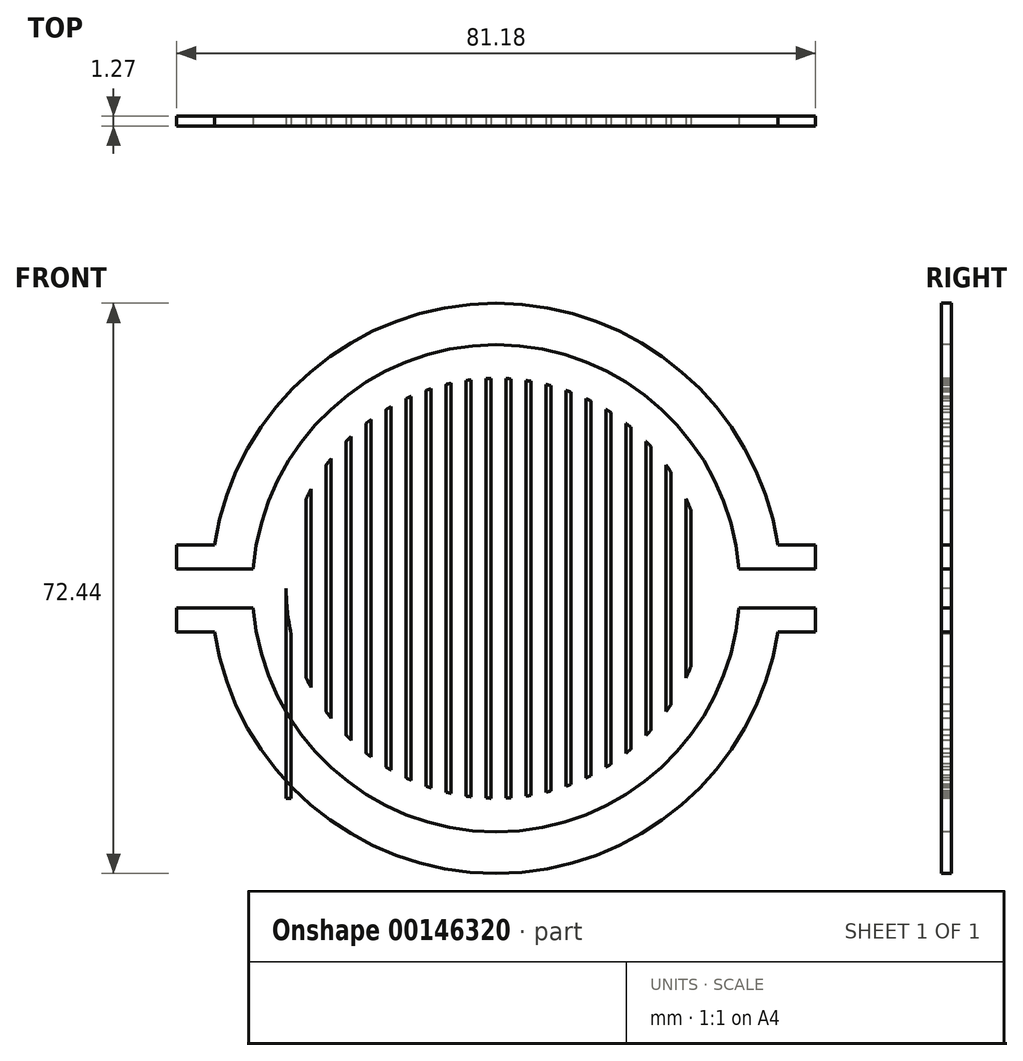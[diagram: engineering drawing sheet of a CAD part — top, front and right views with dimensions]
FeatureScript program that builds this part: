
annotation { "Feature Type Name" : "Feature", "Feature Type Description" : "" }
export const myFeature = defineFeature(function(context is Context, id is Id, definition is map)
    precondition{}
    {
        {
            var Q0;
            Q0=qCreatedBy(makeId("Front.planeOp"),FACE);
            var sketch = newSketch(context, id + "F0", { "sketchPlane" : qUnion([Q0])});
            skPoint(sketch, "E0", {"position": v(0.63, 25.4) * mm});
            skPoint(sketch, "E1", {"position": v(-0.64, 25.4) * mm});
            skLineSegment(sketch, "E2", {"start": v(-0.64, 25.4) * mm, "end": v(0.63, 25.4) * mm});
            skLineSegment(sketch, "E3", {"start": v(0.63, 25.4) * mm, "end": v(0.63, 0.46) * mm});
            skLineSegment(sketch, "E4", {"start": v(-0.64, 25.4) * mm, "end": v(-0.64, 0.2) * mm});
            skPoint(sketch, "E5.1.0", {"position": v(-14.42, 20.92) * mm});
            skLineSegment(sketch, "E5.1.1", {"start": v(-14.42, 20.92) * mm, "end": v(-0.64, 1.95) * mm});
            skLineSegment(sketch, "E5.1.2", {"start": v(-15.44, 20.18) * mm, "end": v(-1.66, 1.2) * mm});
            skPoint(sketch, "E5.1.3", {"position": v(-15.44, 20.18) * mm});
            skLineSegment(sketch, "E5.1.4", {"start": v(-15.44, 20.18) * mm, "end": v(-14.42, 20.92) * mm});
            skPoint(sketch, "E5.2.0", {"position": v(-23.96, 8.45) * mm});
            skLineSegment(sketch, "E5.2.1", {"start": v(-23.96, 8.45) * mm, "end": v(-1.66, 1.2) * mm});
            skLineSegment(sketch, "E5.2.2", {"start": v(-24.35, 7.25) * mm, "end": v(-2.05, 0) * mm});
            skPoint(sketch, "E5.2.3", {"position": v(-24.35, 7.25) * mm});
            skLineSegment(sketch, "E5.2.4", {"start": v(-24.35, 7.25) * mm, "end": v(-23.96, 8.45) * mm});
            skPoint(sketch, "E5.3.0", {"position": v(-24.35, -7.25) * mm});
            skLineSegment(sketch, "E5.3.1", {"start": v(-24.35, -7.25) * mm, "end": v(-2.05, 0) * mm});
            skLineSegment(sketch, "E5.3.2", {"start": v(-23.96, -8.45) * mm, "end": v(-1.66, -1.2) * mm});
            skPoint(sketch, "E5.3.3", {"position": v(-23.96, -8.45) * mm});
            skLineSegment(sketch, "E5.3.4", {"start": v(-23.96, -8.45) * mm, "end": v(-24.35, -7.25) * mm});
            skPoint(sketch, "E5.4.0", {"position": v(-15.44, -20.18) * mm});
            skLineSegment(sketch, "E5.4.1", {"start": v(-15.44, -20.18) * mm, "end": v(-1.66, -1.2) * mm});
            skLineSegment(sketch, "E5.4.2", {"start": v(-14.42, -20.92) * mm, "end": v(-0.63, -1.95) * mm});
            skPoint(sketch, "E5.4.3", {"position": v(-14.42, -20.92) * mm});
            skLineSegment(sketch, "E5.4.4", {"start": v(-14.42, -20.92) * mm, "end": v(-15.44, -20.18) * mm});
            skPoint(sketch, "E5.5.0", {"position": v(-0.64, -25.4) * mm});
            skLineSegment(sketch, "E5.5.1", {"start": v(-0.64, -25.4) * mm, "end": v(-0.63, -1.95) * mm});
            skLineSegment(sketch, "E5.5.2", {"start": v(0.63, -25.4) * mm, "end": v(0.64, -1.95) * mm});
            skPoint(sketch, "E5.5.3", {"position": v(0.63, -25.4) * mm});
            skLineSegment(sketch, "E5.5.4", {"start": v(0.63, -25.4) * mm, "end": v(-0.64, -25.4) * mm});
            skPoint(sketch, "E5.6.0", {"position": v(14.42, -20.92) * mm});
            skLineSegment(sketch, "E5.6.1", {"start": v(14.42, -20.92) * mm, "end": v(0.63, -1.95) * mm});
            skLineSegment(sketch, "E5.6.2", {"start": v(15.44, -20.18) * mm, "end": v(1.66, -1.2) * mm});
            skPoint(sketch, "E5.6.3", {"position": v(15.44, -20.18) * mm});
            skLineSegment(sketch, "E5.6.4", {"start": v(15.44, -20.18) * mm, "end": v(14.42, -20.92) * mm});
            skPoint(sketch, "E5.7.0", {"position": v(23.96, -8.45) * mm});
            skLineSegment(sketch, "E5.7.1", {"start": v(23.96, -8.45) * mm, "end": v(1.66, -1.2) * mm});
            skLineSegment(sketch, "E5.7.2", {"start": v(24.35, -7.25) * mm, "end": v(2.05, 0) * mm});
            skPoint(sketch, "E5.7.3", {"position": v(24.35, -7.25) * mm});
            skLineSegment(sketch, "E5.7.4", {"start": v(24.35, -7.25) * mm, "end": v(23.96, -8.45) * mm});
            skPoint(sketch, "E5.8.0", {"position": v(24.35, 7.25) * mm});
            skLineSegment(sketch, "E5.8.1", {"start": v(24.35, 7.25) * mm, "end": v(2.05, 0) * mm});
            skLineSegment(sketch, "E5.8.2", {"start": v(23.96, 8.45) * mm, "end": v(1.66, 1.2) * mm});
            skPoint(sketch, "E5.8.3", {"position": v(23.96, 8.45) * mm});
            skLineSegment(sketch, "E5.8.4", {"start": v(23.96, 8.45) * mm, "end": v(24.35, 7.25) * mm});
            skPoint(sketch, "E5.9.0", {"position": v(15.44, 20.18) * mm});
            skLineSegment(sketch, "E5.9.1", {"start": v(15.44, 20.18) * mm, "end": v(1.66, 1.2) * mm});
            skLineSegment(sketch, "E5.9.2", {"start": v(14.42, 20.92) * mm, "end": v(0.63, 1.95) * mm});
            skPoint(sketch, "E5.9.3", {"position": v(14.42, 20.92) * mm});
            skLineSegment(sketch, "E5.9.4", {"start": v(14.42, 20.92) * mm, "end": v(15.44, 20.18) * mm});
            skPoint(sketch, "E5.center", {"position": v(0, 0) * mm});
            skLineSegment(sketch, "E6.trimOffspring", {"start": v(0.63, 0.87) * mm, "end": v(0.24, 0.75) * mm});
            skLineSegment(sketch, "E7.trimOffspring", {"start": v(1.03, 0.33) * mm, "end": v(0.78, 0) * mm});
            skLineSegment(sketch, "E8.trimOffspring", {"start": v(1.03, 0.33) * mm, "end": v(0.63, 0.46) * mm});
            skLineSegment(sketch, "E9.trimOffspring", {"start": v(1.03, -0.33) * mm, "end": v(0.64, -0.46) * mm});
            skLineSegment(sketch, "E10.trimOffspring", {"start": v(1.03, -0.33) * mm, "end": v(0.78, 0) * mm});
            skLineSegment(sketch, "E11.trimOffspring", {"start": v(0.64, -0.87) * mm, "end": v(0.24, -0.75) * mm});
            skLineSegment(sketch, "E12.trimOffspring", {"start": v(0.64, -0.87) * mm, "end": v(0.64, -0.46) * mm});
            skLineSegment(sketch, "E13.trimOffspring", {"start": v(0, -1.08) * mm, "end": v(-0.24, -0.75) * mm});
            skLineSegment(sketch, "E14.trimOffspring", {"start": v(0, -1.08) * mm, "end": v(0.24, -0.75) * mm});
            skLineSegment(sketch, "E15.trimOffspring", {"start": v(-0.63, -0.87) * mm, "end": v(-0.63, -0.46) * mm});
            skLineSegment(sketch, "E16.trimOffspring", {"start": v(-0.63, -0.87) * mm, "end": v(-0.24, -0.75) * mm});
            skLineSegment(sketch, "E17.trimOffspring", {"start": v(-1.03, -0.33) * mm, "end": v(-0.78, 0) * mm});
            skLineSegment(sketch, "E18.trimOffspring", {"start": v(-1.03, -0.33) * mm, "end": v(-0.63, -0.46) * mm});
            skLineSegment(sketch, "E19.trimOffspring", {"start": v(-1.03, 0.33) * mm, "end": v(-0.2, 0.6) * mm});
            skLineSegment(sketch, "E20.trimOffspring", {"start": v(-1.03, 0.33) * mm, "end": v(-0.78, 0) * mm});
            skPoint(sketch, "E21.orphan", {"position": v(-0.64, 0) * mm});
            skPoint(sketch, "E22.orphan", {"position": v(0.63, 0) * mm});
            skPoint(sketch, "E23.orphan", {"position": v(0.64, 0) * mm});
            skPoint(sketch, "E24.orphan", {"position": v(0.51, -0.37) * mm});
            skPoint(sketch, "E25.orphan", {"position": v(-0.2, -0.6) * mm});
            skPoint(sketch, "E26.orphan", {"position": v(0.2, -0.6) * mm});
            skPoint(sketch, "E27.orphan", {"position": v(0.51, 0.37) * mm});
            skPoint(sketch, "E28.orphan", {"position": v(-0.51, 0.37) * mm});
            skPoint(sketch, "E29.orphan", {"position": v(-0.51, -0.37) * mm});
            skPoint(sketch, "E30.orphan", {"position": v(-0.2, 0.6) * mm});
            skSolve(sketch);
        }
        {
            var Q0;
            {var subQ6=sQuery(id+"F0.wireOp",EDGE,"E2");Q0=makeQuery(id+"F0.imprint","IMPRINT",FACE,{"disambiguationData":[TD([[makeQuery(id+"F0.imprint","IMPRINT",EDGE,{"derivedFrom":subQ6}),-1.0]])]});}
            var Q1;
            {var subQ1=sQuery(id+"F0.wireOp",EDGE,"E5.1.1");Q1=makeQuery(id+"F0.imprint","IMPRINT",FACE,{"disambiguationData":[TD([[makeQuery(id+"F0.imprint","IMPRINT",EDGE,{"derivedFrom":subQ1}),-1.0]])]});}
            extrude(context, id + "F1", {"entities" : qUnion([Q0, Q1]), "oppositeDirection" : true, "depth" : 50.8 * mm});
        }
        {
            var Q0;
            Q0=qCreatedBy(makeId("Front.planeOp"),FACE);
            var sketch = newSketch(context, id + "F2", { "sketchPlane" : qUnion([Q0])});
            skCircle(sketch, "E31", {"center": v(0, 0) * mm, "radius": 25.4 * mm});
            skCircle(sketch, "E32", {"center": v(0, 0) * mm, "radius": 26.67 * mm});
            skSolve(sketch);
        }
        {
            var Q0;
            Q0=makeQuery(id+"F2.imprint","IMPRINT",FACE,{"disambiguationData":[TD([[makeQuery(id+"F2.imprint","IMPRINT",EDGE,{"derivedFrom":sQuery(id+"F2.wireOp",EDGE,"E31")}),-1.0]])]});
            extrude(context, id + "F3", {"entities" : qUnion([Q0]), "operationType" : NewBodyOperationType.ADD, "oppositeDirection" : true, "depth" : 50.8 * mm});
        }
        {
            var Q0;
            Q0=makeQuery(id+"F3.boolean.opBoolean","MERGE",FACE,{"derivedFrom":[makeQuery(id+"F1.opExtrude","CAP_FACE",FACE,{"disambiguationData":[OSD([sQuery(id+"F0.wireOp",EDGE,"E2"),sQuery(id+"F0.wireOp",EDGE,"E3"),sQuery(id+"F0.wireOp",EDGE,"E4"),sQuery(id+"F0.wireOp",EDGE,"E5.1.1"),sQuery(id+"F0.wireOp",EDGE,"E5.1.2"),sQuery(id+"F0.wireOp",EDGE,"E5.1.4"),sQuery(id+"F0.wireOp",EDGE,"E5.2.1"),sQuery(id+"F0.wireOp",EDGE,"E5.2.2"),sQuery(id+"F0.wireOp",EDGE,"E5.2.4"),sQuery(id+"F0.wireOp",EDGE,"E5.3.1"),sQuery(id+"F0.wireOp",EDGE,"E5.3.2"),sQuery(id+"F0.wireOp",EDGE,"E5.3.4"),sQuery(id+"F0.wireOp",EDGE,"E5.4.1"),sQuery(id+"F0.wireOp",EDGE,"E5.4.2"),sQuery(id+"F0.wireOp",EDGE,"E5.4.4"),sQuery(id+"F0.wireOp",EDGE,"E5.5.1"),sQuery(id+"F0.wireOp",EDGE,"E5.5.2"),sQuery(id+"F0.wireOp",EDGE,"E5.5.4"),sQuery(id+"F0.wireOp",EDGE,"E5.6.1"),sQuery(id+"F0.wireOp",EDGE,"E5.6.2"),sQuery(id+"F0.wireOp",EDGE,"E5.6.4"),sQuery(id+"F0.wireOp",EDGE,"E5.7.1"),sQuery(id+"F0.wireOp",EDGE,"E5.7.2"),sQuery(id+"F0.wireOp",EDGE,"E5.7.4"),sQuery(id+"F0.wireOp",EDGE,"E5.8.1"),sQuery(id+"F0.wireOp",EDGE,"E5.8.2"),sQuery(id+"F0.wireOp",EDGE,"E5.8.4"),sQuery(id+"F0.wireOp",EDGE,"E5.9.1"),sQuery(id+"F0.wireOp",EDGE,"E5.9.2"),sQuery(id+"F0.wireOp",EDGE,"E5.9.4")])],"isStart":false}),makeQuery(id+"F3.opExtrude","CAP_FACE",FACE,{"disambiguationData":[OSD([sQuery(id+"F2.wireOp",EDGE,"E31"),sQuery(id+"F2.wireOp",EDGE,"E32")])],"isStart":false})]});
            var sketch = newSketch(context, id + "F4", { "sketchPlane" : qUnion([Q0])});
            skCircle(sketch, "E33", {"center": v(0, 0) * mm, "radius": 26.67 * mm});
            skCircle(sketch, "E34", {"center": v(0, 0) * mm, "radius": 27.94 * mm});
            skSolve(sketch);
        }
        {
            var Q0;
            Q0=makeQuery(id+"F4.imprint","IMPRINT",FACE,{"disambiguationData":[TD([[makeQuery(id+"F4.imprint","IMPRINT",EDGE,{"derivedFrom":sQuery(id+"F4.wireOp",EDGE,"E33")}),-1.0]])]});
            cPlane(context, id + "F5", {"entities" : qUnion([Q0]), "cplaneType" : CPlaneType.OFFSET, "offset" : 25.4 * mm, "width" : 152.4 * mm, "height" : 152.4 * mm});
        }
        {
            var Q0;
            Q0=qCreatedBy(id+"F5.planeOp",FACE);
            var sketch = newSketch(context, id + "F6", { "sketchPlane" : qUnion([Q0])});
            skCircle(sketch, "E35", {"center": v(0, 0) * mm, "radius": 36.2 * mm});
            skSolve(sketch);
        }
        {
            var Q0;
            Q0=makeQuery(id+"F4.imprint","IMPRINT",FACE,{"disambiguationData":[TD([[makeQuery(id+"F4.imprint","IMPRINT",EDGE,{"derivedFrom":sQuery(id+"F4.wireOp",EDGE,"E33")}),1.0]])]});
            extrude(context, id + "F7", {"entities" : qUnion([Q0]), "endBound" : BoundingType.SYMMETRIC, "depth" : 12.7 * mm});
        }
        {
            var Q0;
            Q0=makeQuery(id+"F6.imprint","IMPRINT",FACE,{"disambiguationData":[TD([[makeQuery(id+"F6.imprint","IMPRINT",EDGE,{"derivedFrom":sQuery(id+"F6.wireOp",EDGE,"E35")}),1.0]])]});
            extrude(context, id + "F8", {"entities" : qUnion([Q0]), "operationType" : NewBodyOperationType.ADD, "oppositeDirection" : true, "depth" : 19.05 * mm});
        }
        {
            var Q0;
            Q0=makeQuery(id+"F8.opExtrude","CAP_EDGE",EDGE,{"disambiguationData":[OSD([sQuery(id+"F6.wireOp",EDGE,"E35")])],"isStart":false});
            chamfer(context, id + "F9", {"entities" : qUnion([Q0]), "width" : 10.16 * mm, "tangentPropagation" : true});
        }
        {
            var Q0;
            Q0=makeQuery(id+"F8.opExtrude","CAP_FACE",FACE,{"disambiguationData":[OSD([sQuery(id+"F6.wireOp",EDGE,"E35")])],"isStart":true});
            shell(context, id + "F10", {"entities" : qUnion([Q0]), "thickness" : 2.54 * mm});
        }
        {
            var Q0;
            Q0=makeQuery(id+"F6.imprint","IMPRINT",FACE,{"disambiguationData":[TD([[makeQuery(id+"F6.imprint","IMPRINT",EDGE,{"derivedFrom":sQuery(id+"F6.wireOp",EDGE,"E35")}),1.0]])]});
            cPlane(context, id + "F11", {"entities" : qUnion([Q0]), "cplaneType" : CPlaneType.OFFSET, "offset" : 16.5 * mm, "oppositeDirection" : true, "width" : 152.4 * mm, "height" : 152.4 * mm});
        }
        {
            var Q0;
            Q0=qCreatedBy(id+"F11.planeOp",FACE);
            var sketch = newSketch(context, id + "F12", { "sketchPlane" : qUnion([Q0])});
            skCircle(sketch, "E36", {"center": v(0, 0) * mm, "radius": 26.67 * mm});
            skSolve(sketch);
        }
        {
            var Q0;
            Q0=qSketchRegion(id+"F12",true);
            extrude(context, id + "F13", {"entities" : qUnion([Q0]), "operationType" : NewBodyOperationType.REMOVE, "oppositeDirection" : true, "depth" : 2.54 * mm});
        }
        {
            var Q0;
            Q0=makeQuery(id+"F3.boolean.opBoolean","MERGE",FACE,{"derivedFrom":[makeQuery(id+"F1.opExtrude","CAP_FACE",FACE,{"disambiguationData":[OSD([sQuery(id+"F0.wireOp",EDGE,"E2"),sQuery(id+"F0.wireOp",EDGE,"E3"),sQuery(id+"F0.wireOp",EDGE,"E4"),sQuery(id+"F0.wireOp",EDGE,"E5.1.1"),sQuery(id+"F0.wireOp",EDGE,"E5.1.2"),sQuery(id+"F0.wireOp",EDGE,"E5.1.4"),sQuery(id+"F0.wireOp",EDGE,"E5.2.1"),sQuery(id+"F0.wireOp",EDGE,"E5.2.2"),sQuery(id+"F0.wireOp",EDGE,"E5.2.4"),sQuery(id+"F0.wireOp",EDGE,"E5.3.1"),sQuery(id+"F0.wireOp",EDGE,"E5.3.2"),sQuery(id+"F0.wireOp",EDGE,"E5.3.4"),sQuery(id+"F0.wireOp",EDGE,"E5.4.1"),sQuery(id+"F0.wireOp",EDGE,"E5.4.2"),sQuery(id+"F0.wireOp",EDGE,"E5.4.4"),sQuery(id+"F0.wireOp",EDGE,"E5.5.1"),sQuery(id+"F0.wireOp",EDGE,"E5.5.2"),sQuery(id+"F0.wireOp",EDGE,"E5.5.4"),sQuery(id+"F0.wireOp",EDGE,"E5.6.1"),sQuery(id+"F0.wireOp",EDGE,"E5.6.2"),sQuery(id+"F0.wireOp",EDGE,"E5.6.4"),sQuery(id+"F0.wireOp",EDGE,"E5.7.1"),sQuery(id+"F0.wireOp",EDGE,"E5.7.2"),sQuery(id+"F0.wireOp",EDGE,"E5.7.4"),sQuery(id+"F0.wireOp",EDGE,"E5.8.1"),sQuery(id+"F0.wireOp",EDGE,"E5.8.2"),sQuery(id+"F0.wireOp",EDGE,"E5.8.4"),sQuery(id+"F0.wireOp",EDGE,"E5.9.1"),sQuery(id+"F0.wireOp",EDGE,"E5.9.2"),sQuery(id+"F0.wireOp",EDGE,"E5.9.4")])],"isStart":true}),makeQuery(id+"F3.opExtrude","CAP_FACE",FACE,{"disambiguationData":[OSD([sQuery(id+"F2.wireOp",EDGE,"E31"),sQuery(id+"F2.wireOp",EDGE,"E32")])],"isStart":true})]});
            cPlane(context, id + "F14", {"entities" : qUnion([Q0]), "cplaneType" : CPlaneType.OFFSET, "offset" : 1.27 * mm, "width" : 152.4 * mm, "height" : 152.4 * mm});
        }
        {
            var Q0;
            Q0=qCreatedBy(id+"F14.planeOp",FACE);
            var sketch = newSketch(context, id + "F15", { "sketchPlane" : qUnion([Q0])});
            skLineSegment(sketch, "E37.bottom", {"start": v(-26.67, 26.67) * mm, "end": v(26.67, 26.67) * mm});
            skLineSegment(sketch, "E37.top", {"start": v(-26.67, -26.67) * mm, "end": v(26.67, -26.67) * mm});
            skLineSegment(sketch, "E37.left", {"start": v(-26.67, 26.67) * mm, "end": v(-26.67, -26.67) * mm});
            skLineSegment(sketch, "E37.right", {"start": v(26.67, 26.67) * mm, "end": v(26.67, -26.67) * mm});
            skPoint(sketch, "E37.middle", {"position": v(0, 0) * mm});
            skPoint(sketch, "E38", {"position": v(-26.03, 26.67) * mm});
            skLineSegment(sketch, "E39", {"start": v(-26.03, 26.67) * mm, "end": v(-26.04, -26.67) * mm});
            skLineSegment(sketch, "E40.MirrorCS", {"start": v(-25.4, 26.67) * mm, "end": v(-25.4, -26.67) * mm});
            skLineSegment(sketch, "E41.MirrorCS", {"start": v(-24.77, 26.67) * mm, "end": v(-24.77, -26.67) * mm});
            skLineSegment(sketch, "E42.MirrorCS", {"start": v(-24.13, 26.67) * mm, "end": v(-24.13, -26.67) * mm});
            skLineSegment(sketch, "E43.MirrorCS", {"start": v(-23.5, 26.67) * mm, "end": v(-23.5, -26.67) * mm});
            skLineSegment(sketch, "E44.MirrorCS", {"start": v(-22.86, 26.67) * mm, "end": v(-22.86, -26.67) * mm});
            skLineSegment(sketch, "E45.MirrorCS", {"start": v(-22.23, 26.67) * mm, "end": v(-22.23, -26.67) * mm});
            skLineSegment(sketch, "E46.MirrorCS", {"start": v(-21.59, 26.67) * mm, "end": v(-21.59, -26.67) * mm});
            skLineSegment(sketch, "E47.MirrorCS", {"start": v(-20.96, 26.67) * mm, "end": v(-20.96, -26.67) * mm});
            skLineSegment(sketch, "E48.MirrorCS", {"start": v(-20.32, 26.67) * mm, "end": v(-20.32, -26.67) * mm});
            skLineSegment(sketch, "E49.MirrorCS", {"start": v(-19.68, 26.67) * mm, "end": v(-19.69, -26.67) * mm});
            skLineSegment(sketch, "E50.MirrorCS", {"start": v(-19.05, 26.67) * mm, "end": v(-19.05, -26.67) * mm});
            skLineSegment(sketch, "E51.MirrorCS", {"start": v(-18.42, 26.67) * mm, "end": v(-18.42, -26.67) * mm});
            skLineSegment(sketch, "E52.MirrorCS", {"start": v(-17.78, 26.67) * mm, "end": v(-17.78, -26.67) * mm});
            skLineSegment(sketch, "E53.MirrorCS", {"start": v(-17.15, 26.67) * mm, "end": v(-17.15, -26.67) * mm});
            skLineSegment(sketch, "E54.MirrorCS", {"start": v(-16.5, 26.67) * mm, "end": v(-16.51, -26.67) * mm});
            skLineSegment(sketch, "E55.MirrorCS", {"start": v(-15.87, 26.67) * mm, "end": v(-15.88, -26.67) * mm});
            skLineSegment(sketch, "E56.MirrorCS", {"start": v(-15.24, 26.67) * mm, "end": v(-15.24, -26.67) * mm});
            skLineSegment(sketch, "E57.MirrorCS", {"start": v(-14.6, 26.67) * mm, "end": v(-14.6, -26.67) * mm});
            skLineSegment(sketch, "E58.MirrorCS", {"start": v(-13.33, 26.67) * mm, "end": v(-13.34, -26.67) * mm});
            skLineSegment(sketch, "E59.MirrorCS", {"start": v(-13.97, 26.67) * mm, "end": v(-13.97, -26.67) * mm});
            skLineSegment(sketch, "E60.MirrorCS", {"start": v(-12.7, 26.67) * mm, "end": v(-12.7, -26.67) * mm});
            skLineSegment(sketch, "E61.MirrorCS", {"start": v(-12.07, 26.67) * mm, "end": v(-12.07, -26.67) * mm});
            skLineSegment(sketch, "E62.MirrorCS", {"start": v(-11.43, 26.67) * mm, "end": v(-11.43, -26.67) * mm});
            skLineSegment(sketch, "E63.MirrorCS", {"start": v(-10.8, 26.67) * mm, "end": v(-10.8, -26.67) * mm});
            skLineSegment(sketch, "E64.MirrorCS", {"start": v(-10.16, 26.67) * mm, "end": v(-10.16, -26.67) * mm});
            skLineSegment(sketch, "E65.MirrorCS", {"start": v(-9.52, 26.67) * mm, "end": v(-9.52, -26.67) * mm});
            skLineSegment(sketch, "E66.MirrorCS", {"start": v(-8.9, 26.67) * mm, "end": v(-8.9, -26.67) * mm});
            skLineSegment(sketch, "E67.MirrorCS", {"start": v(-8.26, 26.67) * mm, "end": v(-8.26, -26.67) * mm});
            skLineSegment(sketch, "E68.MirrorCS", {"start": v(-6.98, 26.67) * mm, "end": v(-6.99, -26.67) * mm});
            skLineSegment(sketch, "E69.MirrorCS", {"start": v(-7.62, 26.67) * mm, "end": v(-7.62, -26.67) * mm});
            skLineSegment(sketch, "E70.MirrorCS", {"start": v(-6.35, 26.67) * mm, "end": v(-6.35, -26.67) * mm});
            skLineSegment(sketch, "E71.MirrorCS", {"start": v(-5.71, 26.67) * mm, "end": v(-5.71, -26.67) * mm});
            skLineSegment(sketch, "E72.MirrorCS", {"start": v(-5.08, 26.67) * mm, "end": v(-5.08, -26.67) * mm});
            skLineSegment(sketch, "E73.MirrorCS", {"start": v(-4.45, 26.67) * mm, "end": v(-4.45, -26.67) * mm});
            skLineSegment(sketch, "E74.MirrorCS", {"start": v(-3.81, 26.67) * mm, "end": v(-3.81, -26.67) * mm});
            skLineSegment(sketch, "E75.MirrorCS", {"start": v(-3.18, 26.67) * mm, "end": v(-3.18, -26.67) * mm});
            skLineSegment(sketch, "E76.MirrorCS", {"start": v(-2.54, 26.67) * mm, "end": v(-2.54, -26.67) * mm});
            skLineSegment(sketch, "E77.MirrorCS", {"start": v(-1.9, 26.67) * mm, "end": v(-1.9, -26.67) * mm});
            skLineSegment(sketch, "E78.MirrorCS", {"start": v(-1.27, 26.67) * mm, "end": v(-1.27, -26.67) * mm});
            skLineSegment(sketch, "E79.MirrorCS", {"start": v(-0.64, 26.67) * mm, "end": v(-0.64, -26.67) * mm});
            skLineSegment(sketch, "E80.MirrorCS", {"start": v(0, 26.67) * mm, "end": v(0, -26.67) * mm});
            skCircle(sketch, "E81", {"center": v(0, 0) * mm, "radius": 26.67 * mm});
            skSolve(sketch);
        }
        {
            var Q0;
            {var subQ0=sQuery(id+"F15.wireOp",EDGE,"E81");var subQ1=sQuery(id+"F15.wireOp",EDGE,"E39");var subQ2=makeQuery(id+"F15.imprint","INTERSECT",VERTEX,{"disambiguationData":[OD(0.0)],"derivedFrom":[subQ1,subQ0]});Q0=makeQuery(id+"F15.imprint","IMPRINT",FACE,{"disambiguationData":[TD([[makeQuery(id+"F15.imprint","IMPRINT",EDGE,{"disambiguationData":[TD([[subQ2,-1.0]])],"derivedFrom":subQ1}),-1.0]])]});}
            var Q1;
            {var subQ0=sQuery(id+"F15.wireOp",EDGE,"E81");var subQ1=sQuery(id+"F15.wireOp",EDGE,"E42.MirrorCS");var subQ2=makeQuery(id+"F15.imprint","INTERSECT",VERTEX,{"disambiguationData":[OD(0.0)],"derivedFrom":[subQ1,subQ0]});Q1=makeQuery(id+"F15.imprint","IMPRINT",FACE,{"disambiguationData":[TD([[makeQuery(id+"F15.imprint","IMPRINT",EDGE,{"disambiguationData":[TD([[subQ2,-1.0]])],"derivedFrom":subQ1}),1.0]])]});}
            var Q2;
            {var subQ0=sQuery(id+"F15.wireOp",EDGE,"E81");var subQ1=sQuery(id+"F15.wireOp",EDGE,"E46.MirrorCS");var subQ2=makeQuery(id+"F15.imprint","INTERSECT",VERTEX,{"disambiguationData":[OD(0.0)],"derivedFrom":[subQ1,subQ0]});Q2=makeQuery(id+"F15.imprint","IMPRINT",FACE,{"disambiguationData":[TD([[makeQuery(id+"F15.imprint","IMPRINT",EDGE,{"disambiguationData":[TD([[subQ2,-1.0]])],"derivedFrom":subQ1}),1.0]])]});}
            var Q3;
            {var subQ0=sQuery(id+"F15.wireOp",EDGE,"E81");var subQ1=sQuery(id+"F15.wireOp",EDGE,"E50.MirrorCS");var subQ2=makeQuery(id+"F15.imprint","INTERSECT",VERTEX,{"disambiguationData":[OD(0.0)],"derivedFrom":[subQ1,subQ0]});Q3=makeQuery(id+"F15.imprint","IMPRINT",FACE,{"disambiguationData":[TD([[makeQuery(id+"F15.imprint","IMPRINT",EDGE,{"disambiguationData":[TD([[subQ2,-1.0]])],"derivedFrom":subQ1}),1.0]])]});}
            var Q4;
            {var subQ0=sQuery(id+"F15.wireOp",EDGE,"E81");var subQ1=sQuery(id+"F15.wireOp",EDGE,"E54.MirrorCS");var subQ2=makeQuery(id+"F15.imprint","INTERSECT",VERTEX,{"disambiguationData":[OD(0.0)],"derivedFrom":[subQ1,subQ0]});Q4=makeQuery(id+"F15.imprint","IMPRINT",FACE,{"disambiguationData":[TD([[makeQuery(id+"F15.imprint","IMPRINT",EDGE,{"disambiguationData":[TD([[subQ2,-1.0]])],"derivedFrom":subQ1}),1.0]])]});}
            var Q5;
            {var subQ0=sQuery(id+"F15.wireOp",EDGE,"E81");var subQ1=sQuery(id+"F15.wireOp",EDGE,"E58.MirrorCS");var subQ2=makeQuery(id+"F15.imprint","INTERSECT",VERTEX,{"disambiguationData":[OD(0.0)],"derivedFrom":[subQ1,subQ0]});Q5=makeQuery(id+"F15.imprint","IMPRINT",FACE,{"disambiguationData":[TD([[makeQuery(id+"F15.imprint","IMPRINT",EDGE,{"disambiguationData":[TD([[subQ2,-1.0]])],"derivedFrom":subQ1}),-1.0]])]});}
            var Q6;
            {var subQ0=sQuery(id+"F15.wireOp",EDGE,"E81");var subQ1=sQuery(id+"F15.wireOp",EDGE,"E62.MirrorCS");var subQ2=makeQuery(id+"F15.imprint","INTERSECT",VERTEX,{"disambiguationData":[OD(0.0)],"derivedFrom":[subQ1,subQ0]});Q6=makeQuery(id+"F15.imprint","IMPRINT",FACE,{"disambiguationData":[TD([[makeQuery(id+"F15.imprint","IMPRINT",EDGE,{"disambiguationData":[TD([[subQ2,-1.0]])],"derivedFrom":subQ1}),1.0]])]});}
            var Q7;
            {var subQ0=sQuery(id+"F15.wireOp",EDGE,"E81");var subQ1=sQuery(id+"F15.wireOp",EDGE,"E66.MirrorCS");var subQ2=makeQuery(id+"F15.imprint","INTERSECT",VERTEX,{"disambiguationData":[OD(0.0)],"derivedFrom":[subQ1,subQ0]});Q7=makeQuery(id+"F15.imprint","IMPRINT",FACE,{"disambiguationData":[TD([[makeQuery(id+"F15.imprint","IMPRINT",EDGE,{"disambiguationData":[TD([[subQ2,-1.0]])],"derivedFrom":subQ1}),1.0]])]});}
            var Q8;
            {var subQ0=sQuery(id+"F15.wireOp",EDGE,"E81");var subQ1=sQuery(id+"F15.wireOp",EDGE,"E70.MirrorCS");var subQ2=makeQuery(id+"F15.imprint","INTERSECT",VERTEX,{"disambiguationData":[OD(0.0)],"derivedFrom":[subQ1,subQ0]});Q8=makeQuery(id+"F15.imprint","IMPRINT",FACE,{"disambiguationData":[TD([[makeQuery(id+"F15.imprint","IMPRINT",EDGE,{"disambiguationData":[TD([[subQ2,-1.0]])],"derivedFrom":subQ1}),1.0]])]});}
            var Q9;
            {var subQ0=sQuery(id+"F15.wireOp",EDGE,"E81");var subQ1=sQuery(id+"F15.wireOp",EDGE,"E74.MirrorCS");var subQ2=makeQuery(id+"F15.imprint","INTERSECT",VERTEX,{"disambiguationData":[OD(0.0)],"derivedFrom":[subQ1,subQ0]});Q9=makeQuery(id+"F15.imprint","IMPRINT",FACE,{"disambiguationData":[TD([[makeQuery(id+"F15.imprint","IMPRINT",EDGE,{"disambiguationData":[TD([[subQ2,-1.0]])],"derivedFrom":subQ1}),1.0]])]});}
            var Q10;
            {var subQ0=sQuery(id+"F15.wireOp",EDGE,"E81");var subQ1=sQuery(id+"F15.wireOp",EDGE,"E79.MirrorCS");var subQ2=makeQuery(id+"F15.imprint","INTERSECT",VERTEX,{"disambiguationData":[OD(0.0)],"derivedFrom":[subQ1,subQ0]});Q10=makeQuery(id+"F15.imprint","IMPRINT",FACE,{"disambiguationData":[TD([[makeQuery(id+"F15.imprint","IMPRINT",EDGE,{"disambiguationData":[TD([[subQ2,-1.0]])],"derivedFrom":subQ1}),-1.0]])]});}
            extrude(context, id + "F16", {"entities" : qUnion([Q0, Q1, Q2, Q3, Q4, Q5, Q6, Q7, Q8, Q9, Q10]), "oppositeDirection" : true, "depth" : 1.27 * mm});
        }
        {
            var Q0;
            Q0=qCreatedBy(id+"F14.planeOp",FACE);
            var sketch = newSketch(context, id + "F17", { "sketchPlane" : qUnion([Q0])});
            skLineSegment(sketch, "E82.bottom", {"start": v(-26.67, 26.67) * mm, "end": v(26.67, 26.67) * mm});
            skLineSegment(sketch, "E82.top", {"start": v(-26.67, -26.67) * mm, "end": v(26.67, -26.67) * mm});
            skLineSegment(sketch, "E82.left", {"start": v(-26.67, 26.67) * mm, "end": v(-26.67, -26.67) * mm});
            skLineSegment(sketch, "E82.right", {"start": v(26.67, 26.67) * mm, "end": v(26.67, -26.67) * mm});
            skPoint(sketch, "E82.middle", {"position": v(0, 0) * mm});
            skCircle(sketch, "E83", {"center": v(0, 0) * mm, "radius": 26.67 * mm});
            skPoint(sketch, "E84", {"position": v(0.63, 26.67) * mm});
            skLineSegment(sketch, "E85", {"start": v(0, 26.67) * mm, "end": v(0, -26.67) * mm});
            skLineSegment(sketch, "E86", {"start": v(0.63, 26.67) * mm, "end": v(0.63, -26.67) * mm});
            skLineSegment(sketch, "E87.MirrorCS", {"start": v(1.27, 26.67) * mm, "end": v(1.27, -26.67) * mm});
            skLineSegment(sketch, "E88.MirrorCS", {"start": v(1.9, 26.67) * mm, "end": v(1.9, -26.67) * mm});
            skLineSegment(sketch, "E89.MirrorCS", {"start": v(2.54, 26.67) * mm, "end": v(2.54, -26.67) * mm});
            skLineSegment(sketch, "E90.MirrorCS", {"start": v(3.17, 26.67) * mm, "end": v(3.17, -26.67) * mm});
            skLineSegment(sketch, "E91.MirrorCS", {"start": v(3.8, 26.67) * mm, "end": v(3.8, -26.67) * mm});
            skLineSegment(sketch, "E92.MirrorCS", {"start": v(4.44, 26.67) * mm, "end": v(4.44, -26.67) * mm});
            skLineSegment(sketch, "E93.MirrorCS", {"start": v(5.08, 26.67) * mm, "end": v(5.08, -26.67) * mm});
            skLineSegment(sketch, "E94.MirrorCS", {"start": v(5.71, 26.67) * mm, "end": v(5.71, -26.67) * mm});
            skLineSegment(sketch, "E95.MirrorCS", {"start": v(6.35, 26.67) * mm, "end": v(6.35, -26.67) * mm});
            skLineSegment(sketch, "E96.MirrorCS", {"start": v(6.98, 26.67) * mm, "end": v(6.98, -26.67) * mm});
            skLineSegment(sketch, "E97.MirrorCS", {"start": v(7.62, 26.67) * mm, "end": v(7.62, -26.67) * mm});
            skLineSegment(sketch, "E98.MirrorCS", {"start": v(8.25, 26.67) * mm, "end": v(8.25, -26.67) * mm});
            skLineSegment(sketch, "E99.MirrorCS", {"start": v(8.89, 26.67) * mm, "end": v(8.89, -26.67) * mm});
            skLineSegment(sketch, "E100.MirrorCS", {"start": v(9.53, 26.67) * mm, "end": v(9.52, -26.67) * mm});
            skLineSegment(sketch, "E101.MirrorCS", {"start": v(10.16, 26.67) * mm, "end": v(10.16, -26.67) * mm});
            skLineSegment(sketch, "E102.MirrorCS", {"start": v(10.8, 26.67) * mm, "end": v(10.8, -26.67) * mm});
            skLineSegment(sketch, "E103.MirrorCS", {"start": v(12.06, 26.67) * mm, "end": v(12.06, -26.67) * mm});
            skLineSegment(sketch, "E104.MirrorCS", {"start": v(12.7, 26.67) * mm, "end": v(12.7, -26.67) * mm});
            skLineSegment(sketch, "E105.MirrorCS", {"start": v(11.43, 26.67) * mm, "end": v(11.43, -26.67) * mm});
            skLineSegment(sketch, "E106.MirrorCS", {"start": v(13.33, 26.67) * mm, "end": v(13.33, -26.67) * mm});
            skLineSegment(sketch, "E107.MirrorCS", {"start": v(13.97, 26.67) * mm, "end": v(13.97, -26.67) * mm});
            skLineSegment(sketch, "E108.MirrorCS", {"start": v(14.6, 26.67) * mm, "end": v(14.6, -26.67) * mm});
            skLineSegment(sketch, "E109.MirrorCS", {"start": v(15.24, 26.67) * mm, "end": v(15.24, -26.67) * mm});
            skLineSegment(sketch, "E110.MirrorCS", {"start": v(15.87, 26.67) * mm, "end": v(15.87, -26.67) * mm});
            skLineSegment(sketch, "E111.MirrorCS", {"start": v(16.5, 26.67) * mm, "end": v(16.5, -26.67) * mm});
            skLineSegment(sketch, "E112.MirrorCS", {"start": v(17.14, 26.67) * mm, "end": v(17.14, -26.67) * mm});
            skLineSegment(sketch, "E113.MirrorCS", {"start": v(17.78, 26.67) * mm, "end": v(17.78, -26.67) * mm});
            skLineSegment(sketch, "E114.MirrorCS", {"start": v(18.41, 26.67) * mm, "end": v(18.41, -26.67) * mm});
            skLineSegment(sketch, "E115.MirrorCS", {"start": v(19.05, 26.67) * mm, "end": v(19.05, -26.67) * mm});
            skLineSegment(sketch, "E116.MirrorCS", {"start": v(19.68, 26.67) * mm, "end": v(19.68, -26.67) * mm});
            skLineSegment(sketch, "E117.MirrorCS", {"start": v(20.32, 26.67) * mm, "end": v(20.32, -26.67) * mm});
            skLineSegment(sketch, "E118.MirrorCS", {"start": v(20.95, 26.67) * mm, "end": v(20.95, -26.67) * mm});
            skLineSegment(sketch, "E119.MirrorCS", {"start": v(21.59, 26.67) * mm, "end": v(21.59, -26.67) * mm});
            skLineSegment(sketch, "E120.MirrorCS", {"start": v(22.22, 26.67) * mm, "end": v(22.22, -26.67) * mm});
            skLineSegment(sketch, "E121.MirrorCS", {"start": v(22.86, 26.67) * mm, "end": v(22.86, -26.67) * mm});
            skLineSegment(sketch, "E122.MirrorCS", {"start": v(23.5, 26.67) * mm, "end": v(23.5, -26.67) * mm});
            skLineSegment(sketch, "E123.MirrorCS", {"start": v(24.13, 26.67) * mm, "end": v(24.13, -26.67) * mm});
            skLineSegment(sketch, "E124.MirrorCS", {"start": v(24.77, 26.67) * mm, "end": v(24.77, -26.67) * mm});
            skLineSegment(sketch, "E125.MirrorCS", {"start": v(25.4, 26.67) * mm, "end": v(25.4, -26.67) * mm});
            skLineSegment(sketch, "E126.MirrorCS", {"start": v(26.03, 26.67) * mm, "end": v(26.03, -26.67) * mm});
            skSolve(sketch);
        }
        {
            var Q0;
            {var subQ0=sQuery(id+"F17.wireOp",EDGE,"E88.MirrorCS");var subQ1=sQuery(id+"F17.wireOp",EDGE,"E83");var subQ2=makeQuery(id+"F17.imprint","INTERSECT",VERTEX,{"disambiguationData":[OD(0.0)],"derivedFrom":[subQ1,subQ0]});Q0=makeQuery(id+"F17.imprint","IMPRINT",FACE,{"disambiguationData":[TD([[makeQuery(id+"F17.imprint","IMPRINT",EDGE,{"disambiguationData":[TD([[subQ2,-1.0]])],"derivedFrom":subQ1}),1.0]])]});}
            var Q1;
            {var subQ0=sQuery(id+"F17.wireOp",EDGE,"E92.MirrorCS");var subQ1=sQuery(id+"F17.wireOp",EDGE,"E83");var subQ2=makeQuery(id+"F17.imprint","INTERSECT",VERTEX,{"disambiguationData":[OD(0.0)],"derivedFrom":[subQ1,subQ0]});Q1=makeQuery(id+"F17.imprint","IMPRINT",FACE,{"disambiguationData":[TD([[makeQuery(id+"F17.imprint","IMPRINT",EDGE,{"disambiguationData":[TD([[subQ2,-1.0]])],"derivedFrom":subQ1}),1.0]])]});}
            var Q2;
            {var subQ0=sQuery(id+"F17.wireOp",EDGE,"E96.MirrorCS");var subQ1=sQuery(id+"F17.wireOp",EDGE,"E83");var subQ2=makeQuery(id+"F17.imprint","INTERSECT",VERTEX,{"disambiguationData":[OD(0.0)],"derivedFrom":[subQ1,subQ0]});Q2=makeQuery(id+"F17.imprint","IMPRINT",FACE,{"disambiguationData":[TD([[makeQuery(id+"F17.imprint","IMPRINT",EDGE,{"disambiguationData":[TD([[subQ2,-1.0]])],"derivedFrom":subQ1}),1.0]])]});}
            var Q3;
            {var subQ0=sQuery(id+"F17.wireOp",EDGE,"E100.MirrorCS");var subQ1=sQuery(id+"F17.wireOp",EDGE,"E83");var subQ2=makeQuery(id+"F17.imprint","INTERSECT",VERTEX,{"disambiguationData":[OD(0.0)],"derivedFrom":[subQ1,subQ0]});Q3=makeQuery(id+"F17.imprint","IMPRINT",FACE,{"disambiguationData":[TD([[makeQuery(id+"F17.imprint","IMPRINT",EDGE,{"disambiguationData":[TD([[subQ2,-1.0]])],"derivedFrom":subQ1}),1.0]])]});}
            var Q4;
            {var subQ0=sQuery(id+"F17.wireOp",EDGE,"E103.MirrorCS");var subQ1=sQuery(id+"F17.wireOp",EDGE,"E83");var subQ2=makeQuery(id+"F17.imprint","INTERSECT",VERTEX,{"disambiguationData":[OD(0.0)],"derivedFrom":[subQ1,subQ0]});Q4=makeQuery(id+"F17.imprint","IMPRINT",FACE,{"disambiguationData":[TD([[makeQuery(id+"F17.imprint","IMPRINT",EDGE,{"disambiguationData":[TD([[subQ2,-1.0]])],"derivedFrom":subQ1}),1.0]])]});}
            var Q5;
            {var subQ0=sQuery(id+"F17.wireOp",EDGE,"E108.MirrorCS");var subQ1=sQuery(id+"F17.wireOp",EDGE,"E83");var subQ2=makeQuery(id+"F17.imprint","INTERSECT",VERTEX,{"disambiguationData":[OD(0.0)],"derivedFrom":[subQ1,subQ0]});Q5=makeQuery(id+"F17.imprint","IMPRINT",FACE,{"disambiguationData":[TD([[makeQuery(id+"F17.imprint","IMPRINT",EDGE,{"disambiguationData":[TD([[subQ2,-1.0]])],"derivedFrom":subQ1}),1.0]])]});}
            var Q6;
            {var subQ0=sQuery(id+"F17.wireOp",EDGE,"E112.MirrorCS");var subQ1=sQuery(id+"F17.wireOp",EDGE,"E83");var subQ2=makeQuery(id+"F17.imprint","INTERSECT",VERTEX,{"disambiguationData":[OD(0.0)],"derivedFrom":[subQ1,subQ0]});Q6=makeQuery(id+"F17.imprint","IMPRINT",FACE,{"disambiguationData":[TD([[makeQuery(id+"F17.imprint","IMPRINT",EDGE,{"disambiguationData":[TD([[subQ2,-1.0]])],"derivedFrom":subQ1}),1.0]])]});}
            var Q7;
            {var subQ0=sQuery(id+"F17.wireOp",EDGE,"E116.MirrorCS");var subQ1=sQuery(id+"F17.wireOp",EDGE,"E83");var subQ2=makeQuery(id+"F17.imprint","INTERSECT",VERTEX,{"disambiguationData":[OD(0.0)],"derivedFrom":[subQ1,subQ0]});Q7=makeQuery(id+"F17.imprint","IMPRINT",FACE,{"disambiguationData":[TD([[makeQuery(id+"F17.imprint","IMPRINT",EDGE,{"disambiguationData":[TD([[subQ2,-1.0]])],"derivedFrom":subQ1}),1.0]])]});}
            var Q8;
            {var subQ0=sQuery(id+"F17.wireOp",EDGE,"E120.MirrorCS");var subQ1=sQuery(id+"F17.wireOp",EDGE,"E83");var subQ2=makeQuery(id+"F17.imprint","INTERSECT",VERTEX,{"disambiguationData":[OD(0.0)],"derivedFrom":[subQ1,subQ0]});Q8=makeQuery(id+"F17.imprint","IMPRINT",FACE,{"disambiguationData":[TD([[makeQuery(id+"F17.imprint","IMPRINT",EDGE,{"disambiguationData":[TD([[subQ2,-1.0]])],"derivedFrom":subQ1}),1.0]])]});}
            var Q9;
            {var subQ0=sQuery(id+"F17.wireOp",EDGE,"E124.MirrorCS");var subQ1=sQuery(id+"F17.wireOp",EDGE,"E83");var subQ2=makeQuery(id+"F17.imprint","INTERSECT",VERTEX,{"disambiguationData":[OD(0.0)],"derivedFrom":[subQ1,subQ0]});Q9=makeQuery(id+"F17.imprint","IMPRINT",FACE,{"disambiguationData":[TD([[makeQuery(id+"F17.imprint","IMPRINT",EDGE,{"disambiguationData":[TD([[subQ2,-1.0]])],"derivedFrom":subQ1}),1.0]])]});}
            extrude(context, id + "F18", {"entities" : qUnion([Q0, Q1, Q2, Q3, Q4, Q5, Q6, Q7, Q8, Q9]), "operationType" : NewBodyOperationType.ADD, "oppositeDirection" : true, "depth" : 1.27 * mm});
        }
        {
            var Q0;
            Q0=qCreatedBy(makeId("Front.planeOp"),FACE);
            cPlane(context, id + "F19", {"entities" : qUnion([Q0]), "cplaneType" : CPlaneType.OFFSET, "offset" : 74.93 * mm, "oppositeDirection" : true, "width" : 152.4 * mm, "height" : 152.4 * mm});
        }
        {
            var Q0;
            Q0=qCreatedBy(id+"F19.planeOp",FACE);
            var sketch = newSketch(context, id + "F20", { "sketchPlane" : qUnion([Q0])});
            skCircle(sketch, "E127", {"center": v(0, 0) * mm, "radius": 36.2 * mm});
            skCircle(sketch, "E128", {"center": v(0, 0) * mm, "radius": 37.47 * mm});
            skSolve(sketch);
        }
        {
            var Q0;
            Q0=makeQuery(id+"F20.imprint","IMPRINT",FACE,{"disambiguationData":[TD([[makeQuery(id+"F20.imprint","IMPRINT",EDGE,{"derivedFrom":sQuery(id+"F20.wireOp",EDGE,"E127")}),-1.0]])]});
            extrude(context, id + "F21", {"entities" : qUnion([Q0]), "depth" : 5.08 * mm});
        }
        {
            var Q0;
            Q0=qCreatedBy(makeId("Right.planeOp"),FACE);
            cPlane(context, id + "F22", {"entities" : qUnion([Q0]), "cplaneType" : CPlaneType.OFFSET, "offset" : 6.35 * mm, "oppositeDirection" : true, "width" : 152.4 * mm, "height" : 152.4 * mm});
        }
        {
            var Q0;
            Q0=qCreatedBy(id+"F22.planeOp",FACE);
            var sketch = newSketch(context, id + "F23", { "sketchPlane" : qUnion([Q0])});
            skCircle(sketch, "E129", {"center": v(72.4, 40.64) * mm, "radius": 3.18 * mm});
            skSolve(sketch);
        }
        {
            var Q0;
            Q0=makeQuery(id+"F23.imprint","IMPRINT",FACE,{"disambiguationData":[TD([[makeQuery(id+"F23.imprint","IMPRINT",EDGE,{"derivedFrom":sQuery(id+"F23.wireOp",EDGE,"E129")}),1.0]])]});
            extrude(context, id + "F24", {"entities" : qUnion([Q0]), "depth" : 12.7 * mm});
        }
        {
            var Q0;
            Q0=makeQuery(id+"F24.opExtrude","CAP_FACE",FACE,{"disambiguationData":[OSD([sQuery(id+"F23.wireOp",EDGE,"E129")])],"isStart":true});
            var sketch = newSketch(context, id + "F25", { "sketchPlane" : qUnion([Q0])});
            skPoint(sketch, "E130", {"position": v(-72.4, 40.64) * mm});
            skPoint(sketch, "E131", {"position": v(-72.4, 41.02) * mm});
            skPoint(sketch, "E132", {"position": v(-72.4, 40.26) * mm});
            skLineSegment(sketch, "E133", {"start": v(-72.4, 41.02) * mm, "end": v(-75.54, 41.02) * mm});
            skLineSegment(sketch, "E134", {"start": v(-75.54, 41.02) * mm, "end": v(-69.24, 41.02) * mm});
            skLineSegment(sketch, "E135", {"start": v(-69.24, 40.27) * mm, "end": v(-75.55, 40.39) * mm});
            skCircle(sketch, "E136", {"center": v(-72.4, 40.64) * mm, "radius": 3.18 * mm});
            skPoint(sketch, "E137.end.orphan", {"position": v(-68.51, 40.26) * mm});
            skSolve(sketch);
        }
        {
            var Q0;
            {var subQ3=sQuery(id+"F25.wireOp",EDGE,"E135");Q0=makeQuery(id+"F25.imprint","IMPRINT",FACE,{"disambiguationData":[TD([[makeQuery(id+"F25.imprint","IMPRINT",EDGE,{"derivedFrom":subQ3}),-1.0]])]});}
            extrude(context, id + "F26", {"entities" : qUnion([Q0]), "operationType" : NewBodyOperationType.REMOVE, "oppositeDirection" : true, "depth" : 1.27 * mm});
        }
        {
            var Q0;
            Q0=makeQuery(id+"F24.opExtrude","CAP_FACE",FACE,{"disambiguationData":[OSD([sQuery(id+"F23.wireOp",EDGE,"E129")])],"isStart":false});
            var sketch = newSketch(context, id + "F27", { "sketchPlane" : qUnion([Q0])});
            skCircle(sketch, "E138", {"center": v(72.4, 40.64) * mm, "radius": 3.17 * mm});
            skCircle(sketch, "E139", {"center": v(72.4, 40.64) * mm, "radius": 1.59 * mm});
            skSolve(sketch);
        }
        {
            var Q0;
            Q0=makeQuery(id+"F27.imprint","IMPRINT",FACE,{"disambiguationData":[TD([[makeQuery(id+"F27.imprint","IMPRINT",EDGE,{"derivedFrom":sQuery(id+"F27.wireOp",EDGE,"E138")}),1.0]])]});
            extrude(context, id + "F28", {"entities" : qUnion([Q0]), "operationType" : NewBodyOperationType.REMOVE, "oppositeDirection" : true, "depth" : 10.16 * mm});
        }
        {
            var Q0;
            Q0=qCreatedBy(id+"F14.planeOp",FACE);
            var sketch = newSketch(context, id + "F29", { "sketchPlane" : qUnion([Q0])});
            skArc(sketch, "E140", {"start": v(-30.85, -2.47) * mm, "mid": v(0, -30.95) * mm, "end": v(30.85, -2.47) * mm});
            skArc(sketch, "E141.trimOffspring", {"start": v(30.85, 2.47) * mm, "mid": v(0, 30.95) * mm, "end": v(-30.85, 2.47) * mm});
            skArc(sketch, "E142", {"start": v(-35.8, -5.53) * mm, "mid": v(0, -36.22) * mm, "end": v(35.8, -5.53) * mm});
            skLineSegment(sketch, "E143", {"start": v(-30.85, 2.47) * mm, "end": v(-40.6, 2.47) * mm});
            skLineSegment(sketch, "E144", {"start": v(-40.6, -2.47) * mm, "end": v(-30.85, -2.47) * mm});
            skLineSegment(sketch, "E145", {"start": v(-36.13, -2.47) * mm, "end": v(-40.6, -2.47) * mm});
            skLineSegment(sketch, "E146.MirrorCS", {"start": v(30.85, 2.47) * mm, "end": v(40.6, 2.47) * mm});
            skLineSegment(sketch, "E147.MirrorCS", {"start": v(40.6, -2.47) * mm, "end": v(30.85, -2.47) * mm});
            skArc(sketch, "E148.trimOffspring", {"start": v(35.8, 5.53) * mm, "mid": v(0, 36.22) * mm, "end": v(-35.8, 5.53) * mm});
            skLineSegment(sketch, "E149", {"start": v(-40.6, 2.47) * mm, "end": v(-40.6, 5.53) * mm});
            skLineSegment(sketch, "E150", {"start": v(-40.6, 5.53) * mm, "end": v(-35.8, 5.53) * mm});
            skLineSegment(sketch, "E151.MirrorCS", {"start": v(40.6, 5.53) * mm, "end": v(35.8, 5.53) * mm});
            skLineSegment(sketch, "E152.MirrorCS", {"start": v(-40.6, -5.53) * mm, "end": v(-35.8, -5.53) * mm});
            skLineSegment(sketch, "E153.MirrorCS", {"start": v(40.6, -5.53) * mm, "end": v(35.8, -5.53) * mm});
            skLineSegment(sketch, "E154", {"start": v(-40.6, -2.47) * mm, "end": v(-40.6, -5.53) * mm});
            skLineSegment(sketch, "E155", {"start": v(40.6, -5.53) * mm, "end": v(40.6, -2.47) * mm});
            skLineSegment(sketch, "E156", {"start": v(40.6, 2.47) * mm, "end": v(40.6, 5.53) * mm});
            skSolve(sketch);
        }
        {
            var Q0;
            Q0=qSketchRegion(id+"F29",true);
            extrude(context, id + "F30", {"entities" : qUnion([Q0]), "oppositeDirection" : true, "depth" : 59.9 * mm});
        }
        {
            var Q0;
            Q0=makeQuery(id+"F30.opExtrude","SWEPT_FACE",FACE,{"disambiguationData":[OSD([sQuery(id+"F29.wireOp",EDGE,"E150")])]});
            var sketch = newSketch(context, id + "F31", { "sketchPlane" : qUnion([Q0])});
            skPoint(sketch, "E157", {"position": v(-38.69, 30.26) * mm});
            skPoint(sketch, "E158", {"position": v(-38.69, 5.8) * mm});
            skPoint(sketch, "E159", {"position": v(-38.69, 50.92) * mm});
            skPoint(sketch, "E160.MirrorP", {"position": v(38.69, 5.8) * mm});
            skPoint(sketch, "E161.MirrorP", {"position": v(38.69, 30.26) * mm});
            skPoint(sketch, "E162.MirrorP", {"position": v(38.69, 50.92) * mm});
            skSolve(sketch);
        }
        {
            var Q0;
            Q0=sQuery(id+"F31.wireOp",VERTEX,"E159");
            var Q1;
            Q1=sQuery(id+"F31.wireOp",VERTEX,"E157");
            var Q2;
            Q2=sQuery(id+"F31.wireOp",VERTEX,"E158");
            var Q3;
            Q3=sQuery(id+"F31.wireOp",VERTEX,"E160.MirrorP");
            var Q4;
            Q4=sQuery(id+"F31.wireOp",VERTEX,"E161.MirrorP");
            var Q5;
            Q5=sQuery(id+"F31.wireOp",VERTEX,"E162.MirrorP");
            var Q6;
            Q6=makeQuery(id+"F30.opExtrude","SWEPT_BODY",BODY,{"disambiguationData":[OSD([sQuery(id+"F29.wireOp",EDGE,"E141.trimOffspring"),sQuery(id+"F29.wireOp",EDGE,"E143"),sQuery(id+"F29.wireOp",EDGE,"E146.MirrorCS"),sQuery(id+"F29.wireOp",EDGE,"E148.trimOffspring"),sQuery(id+"F29.wireOp",EDGE,"E149"),sQuery(id+"F29.wireOp",EDGE,"E150"),sQuery(id+"F29.wireOp",EDGE,"E151.MirrorCS"),sQuery(id+"F29.wireOp",EDGE,"E156")])]});
            hole(context, id + "F32", {"style" : HoleStyle.SIMPLE, "endStyle" : HoleEndStyle.THROUGH, "holeDiameter" : 3.8 * mm, "locations" : qUnion([Q0, Q1, Q2, Q3, Q4, Q5]), "scope" : qUnion([Q6]), "isTappedThrough" : true});
        }
        {
            var Q0;
            Q0=makeQuery(id+"F30.opExtrude","SWEPT_FACE",FACE,{"disambiguationData":[OSD([sQuery(id+"F29.wireOp",EDGE,"E152.MirrorCS")])]});
            var sketch = newSketch(context, id + "F33", { "sketchPlane" : qUnion([Q0])});
            skPoint(sketch, "E163", {"position": v(-38.42, -51.14) * mm});
            skPoint(sketch, "E164.positionSnap0", {"position": v(-40.6, -28.69) * mm});
            skPoint(sketch, "E165", {"position": v(-38.42, -6.03) * mm});
            skPoint(sketch, "E166", {"position": v(-38.42, -30.49) * mm});
            skPoint(sketch, "E167.MirrorP", {"position": v(38.42, -6.03) * mm});
            skPoint(sketch, "E168.MirrorP", {"position": v(38.42, -30.49) * mm});
            skPoint(sketch, "E169.MirrorP", {"position": v(38.42, -51.14) * mm});
            skSolve(sketch);
        }
        {
            var Q0;
            Q0=sQuery(id+"F33.wireOp",VERTEX,"E166");
            var Q1;
            Q1=sQuery(id+"F33.wireOp",VERTEX,"E163");
            var Q2;
            Q2=sQuery(id+"F33.wireOp",VERTEX,"E165");
            var Q3;
            Q3=sQuery(id+"F33.wireOp",VERTEX,"E167.MirrorP");
            var Q4;
            Q4=sQuery(id+"F33.wireOp",VERTEX,"E168.MirrorP");
            var Q5;
            Q5=sQuery(id+"F33.wireOp",VERTEX,"E169.MirrorP");
            var Q6;
            Q6=makeQuery(id+"F30.opExtrude","SWEPT_BODY",BODY,{"disambiguationData":[OSD([sQuery(id+"F29.wireOp",EDGE,"E140"),sQuery(id+"F29.wireOp",EDGE,"E142"),sQuery(id+"F29.wireOp",EDGE,"E144"),sQuery(id+"F29.wireOp",EDGE,"E145"),sQuery(id+"F29.wireOp",EDGE,"E147.MirrorCS"),sQuery(id+"F29.wireOp",EDGE,"E152.MirrorCS"),sQuery(id+"F29.wireOp",EDGE,"E153.MirrorCS"),sQuery(id+"F29.wireOp",EDGE,"E154"),sQuery(id+"F29.wireOp",EDGE,"E155")])]});
            hole(context, id + "F34", {"style" : HoleStyle.SIMPLE, "endStyle" : HoleEndStyle.THROUGH, "holeDiameter" : 3.8 * mm, "locations" : qUnion([Q0, Q1, Q2, Q3, Q4, Q5]), "scope" : qUnion([Q6]), "isTappedThrough" : true});
        }
        {
            var Q0;
            {var subQ0=sQuery(id+"F17.wireOp",EDGE,"E111.MirrorCS");var subQ1=sQuery(id+"F17.wireOp",EDGE,"E83");var subQ2=sQuery(id+"F17.wireOp",EDGE,"E112.MirrorCS");var subQ3=sQuery(id+"F17.wireOp",EDGE,"E107.MirrorCS");var subQ4=sQuery(id+"F17.wireOp",EDGE,"E108.MirrorCS");var subQ5=sQuery(id+"F17.wireOp",EDGE,"E99.MirrorCS");var subQ6=sQuery(id+"F17.wireOp",EDGE,"E100.MirrorCS");var subQ7=sQuery(id+"F17.wireOp",EDGE,"E105.MirrorCS");var subQ8=sQuery(id+"F17.wireOp",EDGE,"E103.MirrorCS");var subQ9=sQuery(id+"F17.wireOp",EDGE,"E95.MirrorCS");var subQ10=sQuery(id+"F17.wireOp",EDGE,"E96.MirrorCS");var subQ11=sQuery(id+"F17.wireOp",EDGE,"E91.MirrorCS");var subQ12=sQuery(id+"F17.wireOp",EDGE,"E92.MirrorCS");var subQ13=sQuery(id+"F17.wireOp",EDGE,"E88.MirrorCS");var subQ14=sQuery(id+"F17.wireOp",EDGE,"E87.MirrorCS");var subQ15=sQuery(id+"F17.wireOp",EDGE,"E124.MirrorCS");var subQ16=sQuery(id+"F17.wireOp",EDGE,"E123.MirrorCS");var subQ17=sQuery(id+"F2.wireOp",EDGE,"E32");var subQ18=sQuery(id+"F17.wireOp",EDGE,"E119.MirrorCS");var subQ19=sQuery(id+"F17.wireOp",EDGE,"E120.MirrorCS");var subQ20=sQuery(id+"F17.wireOp",EDGE,"E115.MirrorCS");var subQ21=sQuery(id+"F17.wireOp",EDGE,"E116.MirrorCS");var subQ22=sQuery(id+"F2.wireOp",EDGE,"E31");Q0=makeQuery(id+"F18.boolean.opBoolean","SPLIT",FACE,{"disambiguationData":[TD([makeQuery(id+"F3.opExtrude","SWEPT_FACE",FACE,{"disambiguationData":[OSD([subQ22])]}),makeQuery(id+"F3.opExtrude","SWEPT_FACE",FACE,{"disambiguationData":[OSD([subQ17])]}),makeQuery(id+"F18.opExtrude","SWEPT_FACE",FACE,{"disambiguationData":[OSD([subQ1]),TDD([makeQuery(id+"F17.imprint","IMPRINT",EDGE,{"disambiguationData":[TD([[makeQuery(id+"F17.imprint","INTERSECT",VERTEX,{"disambiguationData":[OD(0.0)],"derivedFrom":[subQ1,subQ15]}),-1.0]])],"derivedFrom":subQ1})])]}),makeQuery(id+"F18.opExtrude","CAP_FACE",FACE,{"disambiguationData":[OSD([subQ1,subQ16,subQ15])],"isStart":false}),makeQuery(id+"F18.opExtrude","SWEPT_FACE",FACE,{"disambiguationData":[OSD([subQ1]),TDD([makeQuery(id+"F17.imprint","IMPRINT",EDGE,{"disambiguationData":[TD([[makeQuery(id+"F17.imprint","INTERSECT",VERTEX,{"disambiguationData":[OD(0.0)],"derivedFrom":[subQ1,subQ19]}),-1.0]])],"derivedFrom":subQ1})])]}),makeQuery(id+"F18.opExtrude","SWEPT_FACE",FACE,{"disambiguationData":[OSD([subQ1]),TDD([makeQuery(id+"F17.imprint","IMPRINT",EDGE,{"disambiguationData":[TD([[makeQuery(id+"F17.imprint","INTERSECT",VERTEX,{"disambiguationData":[OD(0.0)],"derivedFrom":[subQ1,subQ21]}),-1.0]])],"derivedFrom":subQ1})])]}),makeQuery(id+"F18.opExtrude","SWEPT_FACE",FACE,{"disambiguationData":[OSD([subQ1]),TDD([makeQuery(id+"F17.imprint","IMPRINT",EDGE,{"disambiguationData":[TD([[makeQuery(id+"F17.imprint","INTERSECT",VERTEX,{"disambiguationData":[OD(0.0)],"derivedFrom":[subQ1,subQ2]}),-1.0]])],"derivedFrom":subQ1})])]}),makeQuery(id+"F18.opExtrude","SWEPT_FACE",FACE,{"disambiguationData":[OSD([subQ1]),TDD([makeQuery(id+"F17.imprint","IMPRINT",EDGE,{"disambiguationData":[TD([[makeQuery(id+"F17.imprint","INTERSECT",VERTEX,{"disambiguationData":[OD(0.0)],"derivedFrom":[subQ1,subQ4]}),-1.0]])],"derivedFrom":subQ1})])]}),makeQuery(id+"F18.opExtrude","SWEPT_FACE",FACE,{"disambiguationData":[OSD([subQ1]),TDD([makeQuery(id+"F17.imprint","IMPRINT",EDGE,{"disambiguationData":[TD([[makeQuery(id+"F17.imprint","INTERSECT",VERTEX,{"disambiguationData":[OD(0.0)],"derivedFrom":[subQ1,subQ8]}),-1.0]])],"derivedFrom":subQ1})])]}),makeQuery(id+"F18.opExtrude","SWEPT_FACE",FACE,{"disambiguationData":[OSD([subQ1]),TDD([makeQuery(id+"F17.imprint","IMPRINT",EDGE,{"disambiguationData":[TD([[makeQuery(id+"F17.imprint","INTERSECT",VERTEX,{"disambiguationData":[OD(0.0)],"derivedFrom":[subQ1,subQ6]}),-1.0]])],"derivedFrom":subQ1})])]}),makeQuery(id+"F18.opExtrude","SWEPT_FACE",FACE,{"disambiguationData":[OSD([subQ1]),TDD([makeQuery(id+"F17.imprint","IMPRINT",EDGE,{"disambiguationData":[TD([[makeQuery(id+"F17.imprint","INTERSECT",VERTEX,{"disambiguationData":[OD(0.0)],"derivedFrom":[subQ1,subQ10]}),-1.0]])],"derivedFrom":subQ1})])]}),makeQuery(id+"F18.opExtrude","SWEPT_FACE",FACE,{"disambiguationData":[OSD([subQ1]),TDD([makeQuery(id+"F17.imprint","IMPRINT",EDGE,{"disambiguationData":[TD([[makeQuery(id+"F17.imprint","INTERSECT",VERTEX,{"disambiguationData":[OD(0.0)],"derivedFrom":[subQ1,subQ12]}),-1.0]])],"derivedFrom":subQ1})])]}),makeQuery(id+"F18.opExtrude","SWEPT_FACE",FACE,{"disambiguationData":[OSD([subQ1]),TDD([makeQuery(id+"F17.imprint","IMPRINT",EDGE,{"disambiguationData":[TD([[makeQuery(id+"F17.imprint","INTERSECT",VERTEX,{"disambiguationData":[OD(0.0)],"derivedFrom":[subQ1,subQ13]}),-1.0]])],"derivedFrom":subQ1})])]}),makeQuery(id+"F18.opExtrude","SWEPT_FACE",FACE,{"disambiguationData":[OSD([subQ1]),TDD([makeQuery(id+"F17.imprint","IMPRINT",EDGE,{"disambiguationData":[TD([[makeQuery(id+"F17.imprint","INTERSECT",VERTEX,{"disambiguationData":[OD(1.0)],"derivedFrom":[subQ1,subQ14]}),-1.0]])],"derivedFrom":subQ1})])]}),makeQuery(id+"F18.opExtrude","SWEPT_FACE",FACE,{"disambiguationData":[OSD([subQ1]),TDD([makeQuery(id+"F17.imprint","IMPRINT",EDGE,{"disambiguationData":[TD([[makeQuery(id+"F17.imprint","INTERSECT",VERTEX,{"disambiguationData":[OD(1.0)],"derivedFrom":[subQ1,subQ11]}),-1.0]])],"derivedFrom":subQ1})])]}),makeQuery(id+"F18.opExtrude","SWEPT_FACE",FACE,{"disambiguationData":[OSD([subQ1]),TDD([makeQuery(id+"F17.imprint","IMPRINT",EDGE,{"disambiguationData":[TD([[makeQuery(id+"F17.imprint","INTERSECT",VERTEX,{"disambiguationData":[OD(1.0)],"derivedFrom":[subQ1,subQ9]}),-1.0]])],"derivedFrom":subQ1})])]}),makeQuery(id+"F18.opExtrude","SWEPT_FACE",FACE,{"disambiguationData":[OSD([subQ1]),TDD([makeQuery(id+"F17.imprint","IMPRINT",EDGE,{"disambiguationData":[TD([[makeQuery(id+"F17.imprint","INTERSECT",VERTEX,{"disambiguationData":[OD(1.0)],"derivedFrom":[subQ1,subQ5]}),-1.0]])],"derivedFrom":subQ1})])]}),makeQuery(id+"F18.opExtrude","SWEPT_FACE",FACE,{"disambiguationData":[OSD([subQ1]),TDD([makeQuery(id+"F17.imprint","IMPRINT",EDGE,{"disambiguationData":[TD([[makeQuery(id+"F17.imprint","INTERSECT",VERTEX,{"disambiguationData":[OD(1.0)],"derivedFrom":[subQ1,subQ7]}),-1.0]])],"derivedFrom":subQ1})])]}),makeQuery(id+"F18.opExtrude","SWEPT_FACE",FACE,{"disambiguationData":[OSD([subQ1]),TDD([makeQuery(id+"F17.imprint","IMPRINT",EDGE,{"disambiguationData":[TD([[makeQuery(id+"F17.imprint","INTERSECT",VERTEX,{"disambiguationData":[OD(1.0)],"derivedFrom":[subQ1,subQ3]}),-1.0]])],"derivedFrom":subQ1})])]}),makeQuery(id+"F18.opExtrude","SWEPT_FACE",FACE,{"disambiguationData":[OSD([subQ1]),TDD([makeQuery(id+"F17.imprint","IMPRINT",EDGE,{"disambiguationData":[TD([[makeQuery(id+"F17.imprint","INTERSECT",VERTEX,{"disambiguationData":[OD(1.0)],"derivedFrom":[subQ1,subQ0]}),-1.0]])],"derivedFrom":subQ1})])]}),makeQuery(id+"F18.opExtrude","SWEPT_FACE",FACE,{"disambiguationData":[OSD([subQ1]),TDD([makeQuery(id+"F17.imprint","IMPRINT",EDGE,{"disambiguationData":[TD([[makeQuery(id+"F17.imprint","INTERSECT",VERTEX,{"disambiguationData":[OD(1.0)],"derivedFrom":[subQ1,subQ20]}),-1.0]])],"derivedFrom":subQ1})])]}),makeQuery(id+"F18.opExtrude","SWEPT_FACE",FACE,{"disambiguationData":[OSD([subQ1]),TDD([makeQuery(id+"F17.imprint","IMPRINT",EDGE,{"disambiguationData":[TD([[makeQuery(id+"F17.imprint","INTERSECT",VERTEX,{"disambiguationData":[OD(1.0)],"derivedFrom":[subQ1,subQ18]}),-1.0]])],"derivedFrom":subQ1})])]}),makeQuery(id+"F18.opExtrude","SWEPT_FACE",FACE,{"disambiguationData":[OSD([subQ1]),TDD([makeQuery(id+"F17.imprint","IMPRINT",EDGE,{"disambiguationData":[TD([[makeQuery(id+"F17.imprint","INTERSECT",VERTEX,{"disambiguationData":[OD(1.0)],"derivedFrom":[subQ1,subQ16]}),-1.0]])],"derivedFrom":subQ1})])]}),makeQuery(id+"F18.opExtrude","SWEPT_FACE",FACE,{"disambiguationData":[OSD([subQ15])]})])],"derivedFrom":makeQuery(id+"F3.boolean.opBoolean","MERGE",FACE,{"derivedFrom":[makeQuery(id+"F1.opExtrude","CAP_FACE",FACE,{"disambiguationData":[OSD([sQuery(id+"F0.wireOp",EDGE,"E2"),sQuery(id+"F0.wireOp",EDGE,"E3"),sQuery(id+"F0.wireOp",EDGE,"E4"),sQuery(id+"F0.wireOp",EDGE,"E5.1.1"),sQuery(id+"F0.wireOp",EDGE,"E5.1.2"),sQuery(id+"F0.wireOp",EDGE,"E5.1.4"),sQuery(id+"F0.wireOp",EDGE,"E5.2.1"),sQuery(id+"F0.wireOp",EDGE,"E5.2.2"),sQuery(id+"F0.wireOp",EDGE,"E5.2.4"),sQuery(id+"F0.wireOp",EDGE,"E5.3.1"),sQuery(id+"F0.wireOp",EDGE,"E5.3.2"),sQuery(id+"F0.wireOp",EDGE,"E5.3.4"),sQuery(id+"F0.wireOp",EDGE,"E5.4.1"),sQuery(id+"F0.wireOp",EDGE,"E5.4.2"),sQuery(id+"F0.wireOp",EDGE,"E5.4.4"),sQuery(id+"F0.wireOp",EDGE,"E5.5.1"),sQuery(id+"F0.wireOp",EDGE,"E5.5.2"),sQuery(id+"F0.wireOp",EDGE,"E5.5.4"),sQuery(id+"F0.wireOp",EDGE,"E5.6.1"),sQuery(id+"F0.wireOp",EDGE,"E5.6.2"),sQuery(id+"F0.wireOp",EDGE,"E5.6.4"),sQuery(id+"F0.wireOp",EDGE,"E5.7.1"),sQuery(id+"F0.wireOp",EDGE,"E5.7.2"),sQuery(id+"F0.wireOp",EDGE,"E5.7.4"),sQuery(id+"F0.wireOp",EDGE,"E5.8.1"),sQuery(id+"F0.wireOp",EDGE,"E5.8.2"),sQuery(id+"F0.wireOp",EDGE,"E5.8.4"),sQuery(id+"F0.wireOp",EDGE,"E5.9.1"),sQuery(id+"F0.wireOp",EDGE,"E5.9.2"),sQuery(id+"F0.wireOp",EDGE,"E5.9.4")])],"isStart":true}),makeQuery(id+"F3.opExtrude","CAP_FACE",FACE,{"disambiguationData":[OSD([subQ22,subQ17])],"isStart":true})]})});}
            var sketch = newSketch(context, id + "F35", { "sketchPlane" : qUnion([Q0])});
            skLineSegment(sketch, "E170.bottom", {"start": v(-71.98, -60.1) * mm, "end": v(99.36, -60.1) * mm});
            skLineSegment(sketch, "E170.top", {"start": v(-71.98, 79.11) * mm, "end": v(99.36, 79.11) * mm});
            skLineSegment(sketch, "E170.left", {"start": v(-71.98, -60.1) * mm, "end": v(-71.98, 79.11) * mm});
            skLineSegment(sketch, "E170.right", {"start": v(99.36, -60.1) * mm, "end": v(99.36, 79.11) * mm});
            skSolve(sketch);
        }
        {
            var Q0;
            Q0 = qSketchRegion(id + "F35", true);
            extrude(context, id + "F36", {"entities" : qUnion([Q0]), "operationType" : NewBodyOperationType.REMOVE, "oppositeDirection" : true, "depth" : 254 * mm});
        }
    });
